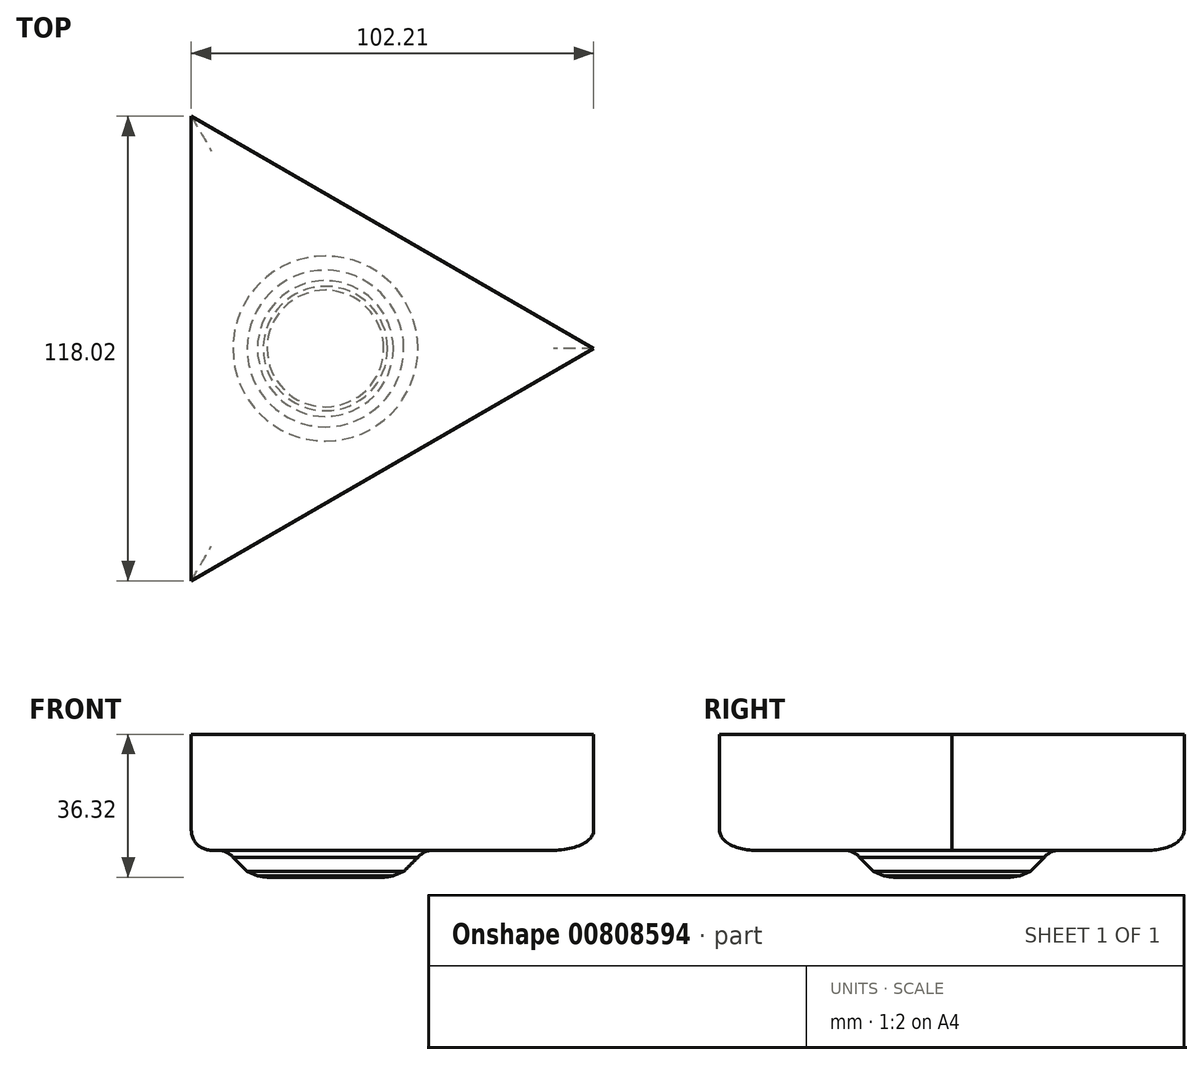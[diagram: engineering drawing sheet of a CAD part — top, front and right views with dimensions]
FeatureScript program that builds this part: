
annotation { "Feature Type Name" : "Feature", "Feature Type Description" : "" }
export const myFeature = defineFeature(function(context is Context, id is Id, definition is map)
    precondition{}
    {
        {
            var Q0;
            Q0=qCreatedBy(makeId("Top.planeOp"),FACE);
            var sketch = newSketch(context, id + "F0", { "sketchPlane" : qUnion([Q0])});
            skCircle(sketch, "E0.cCircle", {"center": v(0, 0) * mm, "radius": 34.07 * mm, "construction": true});
            skLineSegment(sketch, "E0.0", {"start": v(-34.07, -59.01) * mm, "end": v(-34.07, 59.01) * mm});
            skLineSegment(sketch, "E0.1", {"start": v(-34.07, 59.01) * mm, "end": v(68.14, 0) * mm});
            skLineSegment(sketch, "E0.2", {"start": v(68.14, 0) * mm, "end": v(-34.07, -59.01) * mm});
            skPoint(sketch, "E0.0.midPoint", {"position": v(-34.07, 0) * mm});
            skSolve(sketch);
        }
        {
            var Q0;
            Q0 = qSketchRegion(id + "F0", true);
            extrude(context, id + "F1", {"entities" : qUnion([Q0]), "depth" : 29.46 * mm, "offsetDistance" : 25.4 * mm});
        }
        {
            var Q0;
            Q0=makeQuery(id+"F1.opExtrude","CAP_FACE",FACE,{"disambiguationData":[OSD([sQuery(id+"F0.wireOp",EDGE,"E0.0"),sQuery(id+"F0.wireOp",EDGE,"E0.1"),sQuery(id+"F0.wireOp",EDGE,"E0.2")])],"isStart":false});
            var sketch = newSketch(context, id + "F2", { "sketchPlane" : qUnion([Q0])});
            skCircle(sketch, "E1", {"center": v(0, 0) * mm, "radius": 23.5 * mm});
            skSolve(sketch);
        }
        {
            var Q0;
            Q0 = qSketchRegion(id + "F2", true);
            extrude(context, id + "F3", {"entities" : qUnion([Q0]), "operationType" : NewBodyOperationType.ADD, "oppositeDirection" : true, "depth" : 36.32 * mm, "offsetDistance" : 25.4 * mm});
        }
        {
            var Q0;
            Q0=makeQuery(id+"F3.opExtrude","CAP_FACE",FACE,{"disambiguationData":[OSD([sQuery(id+"F2.wireOp",EDGE,"E1")])],"isStart":false});
            chamfer(context, id + "F4", {"entities" : qUnion([Q0]), "width" : 5.08 * mm, "tangentPropagation" : true});
        }
        {
            var Q0;
            Q0=makeQuery(id+"F1.opExtrude","CAP_FACE",FACE,{"disambiguationData":[OSD([sQuery(id+"F0.wireOp",EDGE,"E0.0"),sQuery(id+"F0.wireOp",EDGE,"E0.1"),sQuery(id+"F0.wireOp",EDGE,"E0.2")])],"isStart":true});
            fillet(context, id + "F5", {"entities" : qUnion([Q0]), "radius" : 5.08 * mm, "tangentPropagation" : true, "allowEdgeOverflow" : false});
        }
        {
            var Q0;
            Q0=makeQuery(id+"F3.opExtrude","CAP_FACE",FACE,{"disambiguationData":[OSD([sQuery(id+"F2.wireOp",EDGE,"E1")])],"isStart":false});
            chamfer(context, id + "F6", {"entities" : qUnion([Q0]), "width" : 5.08 * mm, "tangentPropagation" : true});
        }
        {
            var Q0;
            Q0=makeQuery(id+"F3.opExtrude","CAP_FACE",FACE,{"disambiguationData":[OSD([sQuery(id+"F2.wireOp",EDGE,"E1")])],"isStart":false});
            chamfer(context, id + "F7", {"entities" : qUnion([Q0]), "width" : 5.08 * mm, "tangentPropagation" : true});
        }
        {
            var Q0;
            Q0=makeQuery(id+"F3.opExtrude","CAP_FACE",FACE,{"disambiguationData":[OSD([sQuery(id+"F2.wireOp",EDGE,"E1")])],"isStart":false});
            chamfer(context, id + "F8", {"entities" : qUnion([Q0]), "width" : 5.08 * mm, "tangentPropagation" : true});
        }
    });
